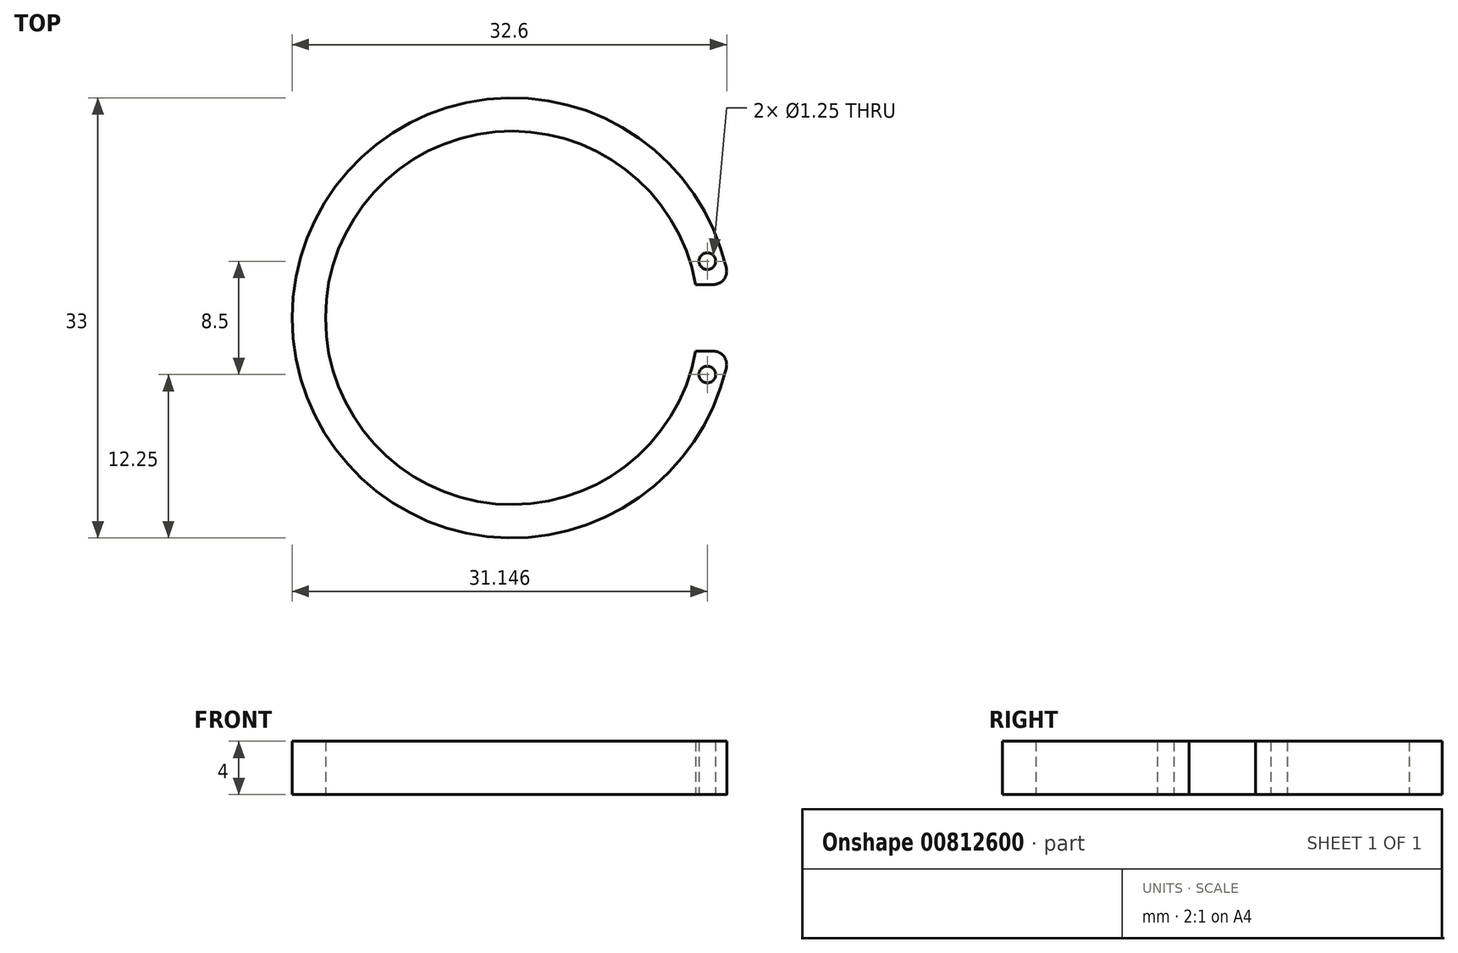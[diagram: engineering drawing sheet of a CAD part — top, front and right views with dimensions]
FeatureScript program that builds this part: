
annotation { "Feature Type Name" : "Feature", "Feature Type Description" : "" }
export const myFeature = defineFeature(function(context is Context, id is Id, definition is map)
    precondition{}
    {
        {
            var Q0;
            Q0=qCreatedBy(makeId("Top.planeOp"),FACE);
            var sketch = newSketch(context, id + "F0", { "sketchPlane" : qUnion([Q0])});
            skArc(sketch, "E0", {"start": v(13.77, 2.5) * mm, "mid": v(-14, 0) * mm, "end": v(13.77, -2.5) * mm});
            skArc(sketch, "E1", {"start": v(16.3, 2.5) * mm, "mid": v(-16.5, 0) * mm, "end": v(16.3, -2.5) * mm});
            skLineSegment(sketch, "E2.bottom", {"start": v(13.77, 2.5) * mm, "end": v(16.3, 2.5) * mm});
            skLineSegment(sketch, "E2.top", {"start": v(13.77, -2.5) * mm, "end": v(16.3, -2.5) * mm});
            skCircle(sketch, "E3", {"center": v(0, 0) * mm, "radius": 15.25 * mm, "construction": true});
            skCircle(sketch, "E4", {"center": v(14.65, 4.25) * mm, "radius": 0.62 * mm});
            skCircle(sketch, "E5.MirrorC", {"center": v(14.65, -4.25) * mm, "radius": 0.62 * mm});
            skSolve(sketch);
        }
        {
            var Q0;
            Q0 = qSketchRegion(id + "F0", true);
            extrude(context, id + "F1", {"entities" : qUnion([Q0]), "depth" : 4 * mm, "offsetDistance" : 25 * mm});
        }
        {
            var Q0;
            Q0=makeQuery(id+"F1.opExtrude","SWEPT_EDGE",EDGE,{"disambiguationData":[OSD([sQuery(id+"F0.wireOp",EDGE,"E1"),sQuery(id+"F0.wireOp",EDGE,"E2.bottom")])]});
            var Q1;
            Q1=makeQuery(id+"F1.opExtrude","SWEPT_EDGE",EDGE,{"disambiguationData":[OSD([sQuery(id+"F0.wireOp",EDGE,"E1"),sQuery(id+"F0.wireOp",EDGE,"E2.top")])]});
            fillet(context, id + "F2", {"entities" : qUnion([Q0, Q1]), "radius" : 1 * mm, "tangentPropagation" : true, "allowEdgeOverflow" : false});
        }
    });
